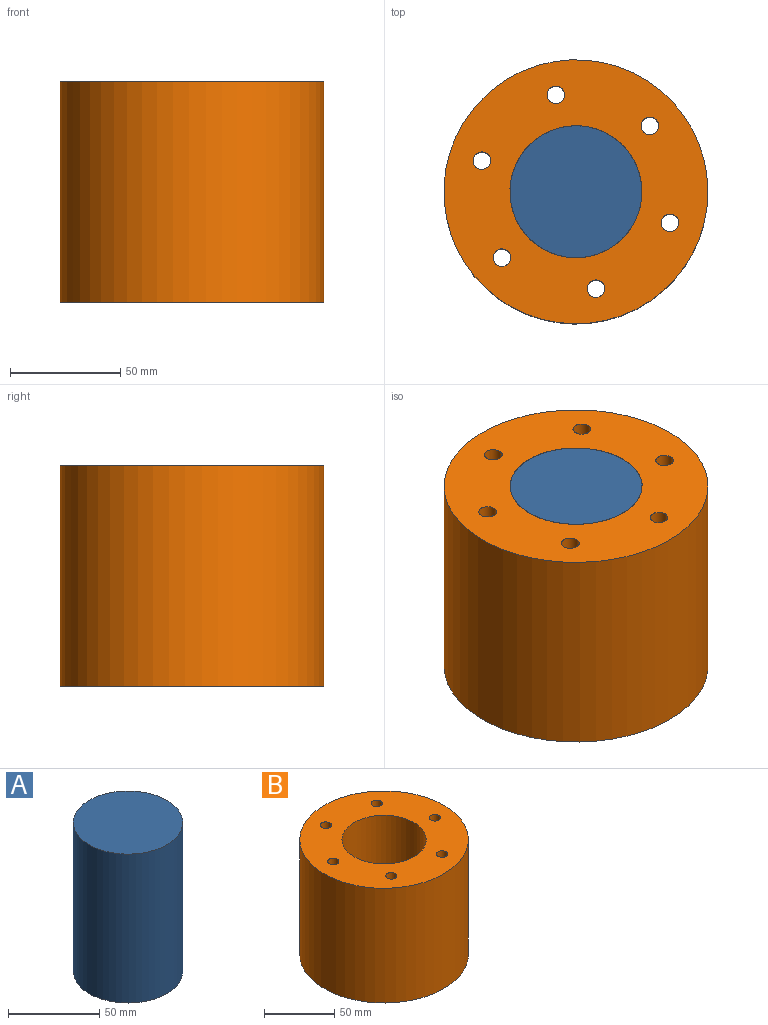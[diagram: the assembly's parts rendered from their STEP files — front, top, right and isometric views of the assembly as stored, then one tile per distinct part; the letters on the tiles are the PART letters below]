
ASSEMBLY  parts=2 mates=1
PART A: 3 faces, bbox 60x60x100 mm
  f0: cylinder r=30mm len=100mm, axis (0,0,-1), area 18849.6mm2, adj f1,f2
  f1: plane 60x60mm, normal (0,0,1), area 2827.4mm2, adj f0
  f2: plane 60x60mm, normal (0,0,-1), area 2827.4mm2, adj f0
PART B: 10 faces, bbox 120x120x100 mm
  f0: cylinder r=30mm len=100mm, axis (0,0,-1), area 18849.6mm2, adj f2,f3
  f1: cylinder r=60mm len=120mm, axis (0,0,-1), area 37699.1mm2, adj f2,f3
  f2: plane 120x120mm, normal (0,0,1), area 8180.7mm2, adj f0,f1,f4,f5,f6,f7,f8,f9
  f3: plane 120x120mm, normal (0,0,-1), area 8180.7mm2, adj f0,f1,f4,f5,f6,f7,f8,f9
  f4: cylinder r=4mm len=100mm, axis (0,0,1), area 2513.3mm2, adj f2,f3
  f5: cylinder r=4mm len=100mm, axis (0,0,1), area 2513.3mm2, adj f2,f3
  f6: cylinder r=4mm len=100mm, axis (0,0,1), area 2513.3mm2, adj f2,f3
  f7: cylinder r=4mm len=100mm, axis (0,0,1), area 2513.3mm2, adj f2,f3
  f8: cylinder r=4mm len=100mm, axis (0,0,1), area 2513.3mm2, adj f2,f3
  f9: cylinder r=4mm len=100mm, axis (0,0,1), area 2513.3mm2, adj f2,f3
PLACE A t=(-31.09,14.68,-1.06)mm fixed
PLACE B rot(axis=(0,0,1),170deg) t=(78.73,91.28,-1.06)mm
MATE revolute A.f0 <-> B.f0  axis (0,0,1) through (-31.09,14.68,98.94)mm
